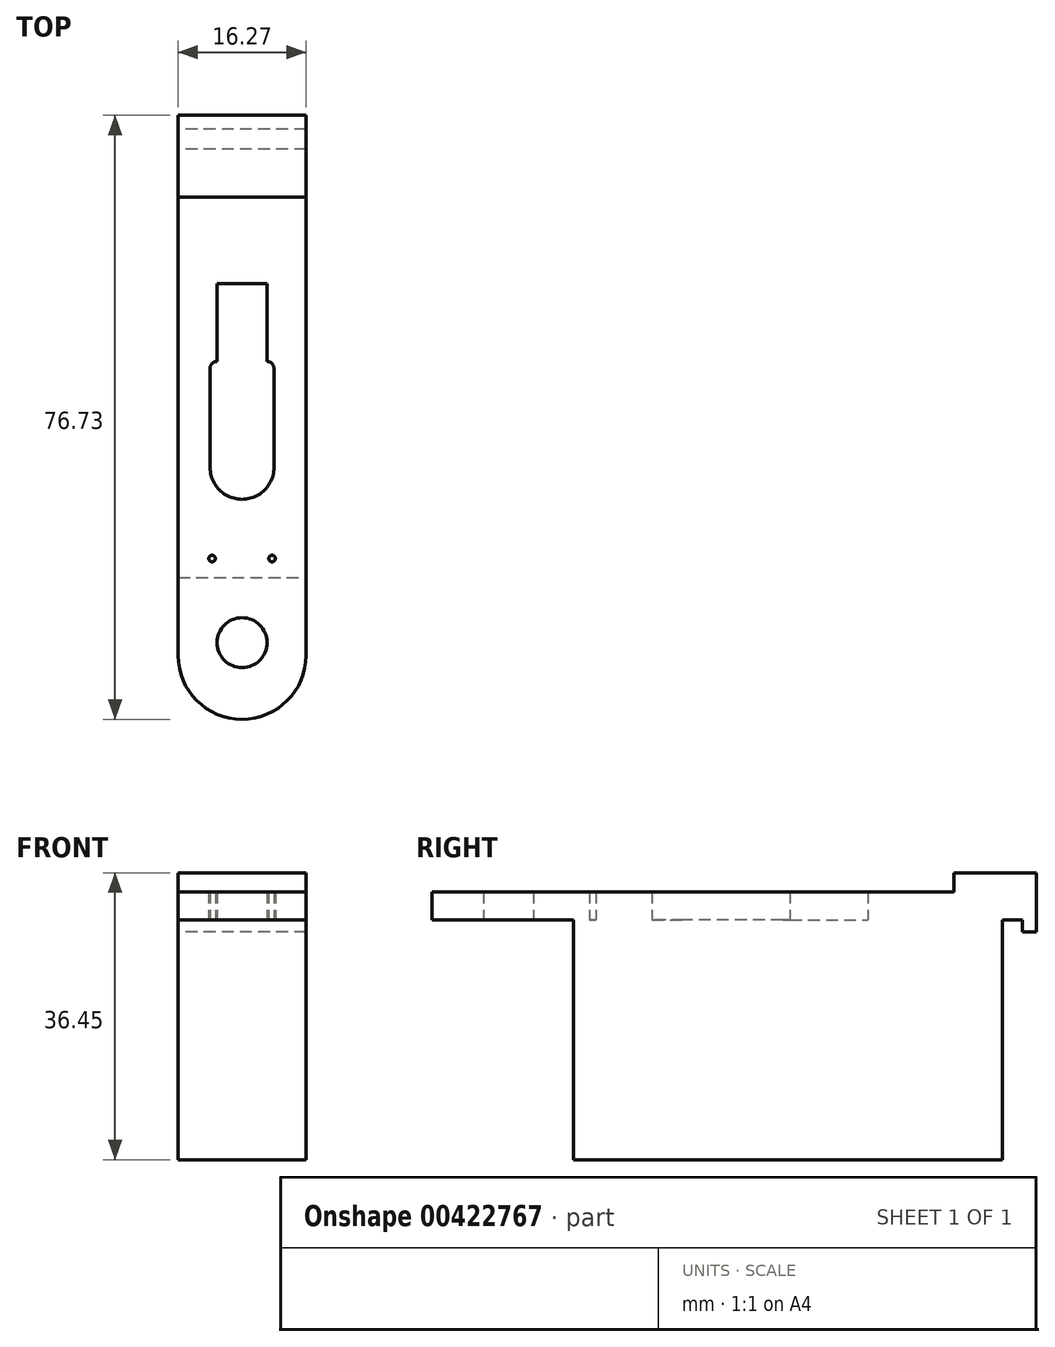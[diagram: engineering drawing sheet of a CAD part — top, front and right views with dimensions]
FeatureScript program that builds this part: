
annotation { "Feature Type Name" : "Feature", "Feature Type Description" : "" }
export const myFeature = defineFeature(function(context is Context, id is Id, definition is map)
    precondition{}
    {
        {
            var Q0;
            Q0=qCreatedBy(makeId("Top.planeOp"),FACE);
            var sketch = newSketch(context, id + "F0", { "sketchPlane" : qUnion([Q0])});
            skArc(sketch, "E0", {"start": v(-8.13, -38.64) * mm, "mid": v(0, -46.76) * mm, "end": v(8.13, -38.64) * mm});
            skCircle(sketch, "E1", {"center": v(0, -37.04) * mm, "radius": 3.18 * mm});
            skLineSegment(sketch, "E2", {"start": v(-8.13, -28.78) * mm, "end": v(8.13, -28.78) * mm});
            skCircle(sketch, "E3", {"center": v(3.81, -26.34) * mm, "radius": 0.42 * mm});
            skCircle(sketch, "E4", {"center": v(-3.8, -26.34) * mm, "radius": 0.42 * mm});
            skLineSegment(sketch, "E5", {"start": v(-8.13, -38.64) * mm, "end": v(-8.13, -28.78) * mm});
            skLineSegment(sketch, "E6", {"start": v(8.13, -38.64) * mm, "end": v(8.13, -28.78) * mm});
            skLineSegment(sketch, "E7", {"start": v(8.13, 19.54) * mm, "end": v(8.13, -28.78) * mm});
            skLineSegment(sketch, "E8", {"start": v(8.13, 19.54) * mm, "end": v(8.14, 25.65) * mm});
            skLineSegment(sketch, "E9", {"start": v(8.14, 25.65) * mm, "end": v(8.14, 28.2) * mm});
            skLineSegment(sketch, "E10", {"start": v(8.14, 28.2) * mm, "end": v(8.14, 29.97) * mm});
            skLineSegment(sketch, "E11", {"start": v(8.13, 19.54) * mm, "end": v(-8.13, 19.57) * mm});
            skLineSegment(sketch, "E12", {"start": v(8.14, 25.65) * mm, "end": v(-8.13, 25.65) * mm});
            skLineSegment(sketch, "E13", {"start": v(8.14, 28.2) * mm, "end": v(-8.13, 28.2) * mm});
            skLineSegment(sketch, "E14", {"start": v(8.14, 29.97) * mm, "end": v(-8.13, 29.97) * mm});
            skLineSegment(sketch, "E15", {"start": v(-8.13, -28.78) * mm, "end": v(-8.13, 19.57) * mm});
            skLineSegment(sketch, "E16", {"start": v(-8.13, 19.57) * mm, "end": v(-8.13, 25.65) * mm});
            skLineSegment(sketch, "E17", {"start": v(-8.13, 25.65) * mm, "end": v(-8.13, 28.2) * mm});
            skLineSegment(sketch, "E18", {"start": v(-8.13, 28.2) * mm, "end": v(-8.13, 29.97) * mm});
            skArc(sketch, "E19.0.1.0", {"start": v(-4.06, -14.76) * mm, "mid": v(0, -18.82) * mm, "end": v(4.06, -14.75) * mm});
            skLineSegment(sketch, "E19.0.1.1", {"start": v(-4.07, -2.19) * mm, "end": v(-4.06, -14.76) * mm});
            skLineSegment(sketch, "E19.0.1.2", {"start": v(4.05, -2.19) * mm, "end": v(4.06, -14.75) * mm});
            skArc(sketch, "E19.0.1.3", {"start": v(-3.18, -1.3) * mm, "mid": v(-3.8, -1.56) * mm, "end": v(-4.07, -2.19) * mm});
            skLineSegment(sketch, "E19.0.1.4", {"start": v(-3.18, -1.3) * mm, "end": v(-3.18, 8.6) * mm});
            skArc(sketch, "E19.0.1.5", {"start": v(4.05, -2.19) * mm, "mid": v(3.8, -1.56) * mm, "end": v(3.17, -1.3) * mm});
            skLineSegment(sketch, "E19.0.1.6", {"start": v(3.17, -1.3) * mm, "end": v(3.17, 8.6) * mm});
            skLineSegment(sketch, "E19.0.1.7", {"start": v(3.17, 8.6) * mm, "end": v(-3.18, 8.6) * mm});
            skSolve(sketch);
        }
        {
            var Q0;
            Q0=makeQuery(id+"F0.imprint","IMPRINT",FACE,{"disambiguationData":[TD([[makeQuery(id+"F0.imprint","IMPRINT",EDGE,{"derivedFrom":sQuery(id+"F0.wireOp",EDGE,"E2")}),1.0]])]});
            var Q1;
            Q1=makeQuery(id+"F0.imprint","IMPRINT",FACE,{"disambiguationData":[TD([[makeQuery(id+"F0.imprint","IMPRINT",EDGE,{"derivedFrom":sQuery(id+"F0.wireOp",EDGE,"E0")}),1.0]])]});
            extrude(context, id + "F1", {"entities" : qUnion([Q0, Q1]), "depth" : 3.56 * mm, "offsetDistance" : 25.4 * mm});
        }
        {
            var Q0;
            Q0=makeQuery(id+"F0.imprint","IMPRINT",FACE,{"disambiguationData":[TD([[makeQuery(id+"F0.imprint","IMPRINT",EDGE,{"derivedFrom":sQuery(id+"F0.wireOp",EDGE,"E8")}),1.0]])]});
            var Q1;
            Q1=makeQuery(id+"F0.imprint","IMPRINT",FACE,{"disambiguationData":[TD([[makeQuery(id+"F0.imprint","IMPRINT",EDGE,{"derivedFrom":sQuery(id+"F0.wireOp",EDGE,"E9")}),1.0]])]});
            var Q2;
            Q2=makeQuery(id+"F0.imprint","IMPRINT",FACE,{"disambiguationData":[TD([[makeQuery(id+"F0.imprint","IMPRINT",EDGE,{"derivedFrom":sQuery(id+"F0.wireOp",EDGE,"E10")}),1.0]])]});
            extrude(context, id + "F2", {"entities" : qUnion([Q0, Q1, Q2]), "operationType" : NewBodyOperationType.ADD, "depth" : 5.97 * mm, "offsetDistance" : 25.4 * mm});
        }
        {
            var Q0;
            Q0=makeQuery(id+"F0.imprint","IMPRINT",FACE,{"disambiguationData":[TD([[makeQuery(id+"F0.imprint","IMPRINT",EDGE,{"derivedFrom":sQuery(id+"F0.wireOp",EDGE,"E10")}),1.0]])]});
            extrude(context, id + "F3", {"entities" : qUnion([Q0]), "operationType" : NewBodyOperationType.ADD, "oppositeDirection" : true, "depth" : 1.52 * mm, "offsetDistance" : 25.4 * mm});
        }
        {
            var Q0;
            Q0=makeQuery(id+"F0.imprint","IMPRINT",FACE,{"disambiguationData":[TD([[makeQuery(id+"F0.imprint","IMPRINT",EDGE,{"derivedFrom":sQuery(id+"F0.wireOp",EDGE,"E8")}),1.0]])]});
            var Q1;
            Q1=makeQuery(id+"F0.imprint","IMPRINT",FACE,{"disambiguationData":[TD([[makeQuery(id+"F0.imprint","IMPRINT",EDGE,{"derivedFrom":sQuery(id+"F0.wireOp",EDGE,"E3")}),1.0]])]});
            var Q2;
            Q2=makeQuery(id+"F0.imprint","IMPRINT",FACE,{"disambiguationData":[TD([[makeQuery(id+"F0.imprint","IMPRINT",EDGE,{"derivedFrom":sQuery(id+"F0.wireOp",EDGE,"E2")}),1.0]])]});
            var Q3;
            Q3=makeQuery(id+"F0.imprint","IMPRINT",FACE,{"disambiguationData":[TD([[makeQuery(id+"F0.imprint","IMPRINT",EDGE,{"derivedFrom":sQuery(id+"F0.wireOp",EDGE,"E4")}),1.0]])]});
            var Q4;
            Q4=makeQuery(id+"F0.imprint","IMPRINT",FACE,{"disambiguationData":[TD([[makeQuery(id+"F0.imprint","IMPRINT",EDGE,{"derivedFrom":sQuery(id+"F0.wireOp",EDGE,"E19.0.1.0")}),1.0]])]});
            extrude(context, id + "F4", {"entities" : qUnion([Q0, Q1, Q2, Q3, Q4]), "operationType" : NewBodyOperationType.ADD, "oppositeDirection" : true, "depth" : 30.48 * mm, "offsetDistance" : 25.4 * mm});
        }
    });
